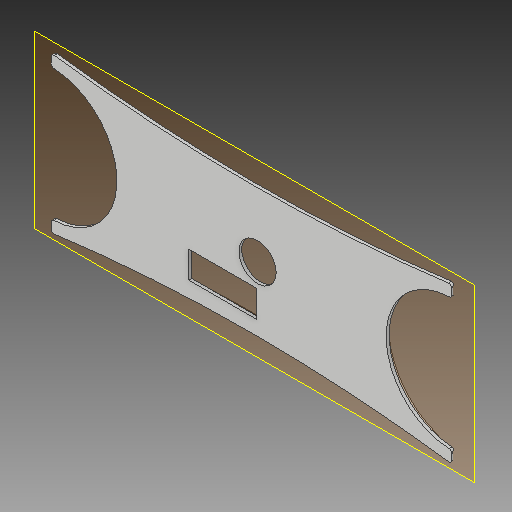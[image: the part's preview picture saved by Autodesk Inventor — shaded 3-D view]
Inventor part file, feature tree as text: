
AUTODESK INVENTOR PART (.ipt)
format: ipt  version: 2017 (Build 210142000, 142)  size: 173,056 bytes
history: native  units: mm
features: reference x5, extrude x3, sketch x3, other x3, plane x1, fillet x1
ambient origin geometry x8: Origin, YZ Plane, XZ Plane, XY Plane, X Axis, Y Axis, Z Axis, Center Point
bodies: Solid1 (feature_tree)
feature tree (16):
  plane  "Work Plane1"
  extrude  "Extrusion1"  Depth=1.0mm
  fillet  "Fillet1"  Radius=0.1mm
  extrude  "Extrusion2"  Depth=2.0mm TaperAngle=0.0deg
  extrude  "Extrusion3"  Depth=1.0mm
  sketch  "Sketch1"  dims[d0=1.0mm d1=0.0mm d2=1.0mm d3=0.1mm]
  reference  "Reference1"
  sketch  "Sketch2"  dims[d4=1.0mm d5=2.0mm d6=0.0mm]
  reference  "Reference2"
  reference  "Reference3"
  reference  "Reference4"
  reference  "Reference5"
  sketch  "Sketch3"  dims[d7=0.25mm d8=0.25mm d9=1.0mm d10=0.0mm d11=1.0mm]
  parser-record x1  (decoder bookkeeping rows leaked as tree rows — omitted from the tree; the rows remain in map.json)
  other  "assembly_full.iam"
  other  "base:1"
note: 1 file-system path scrubbed to <path> (originals preserved in map.json)
